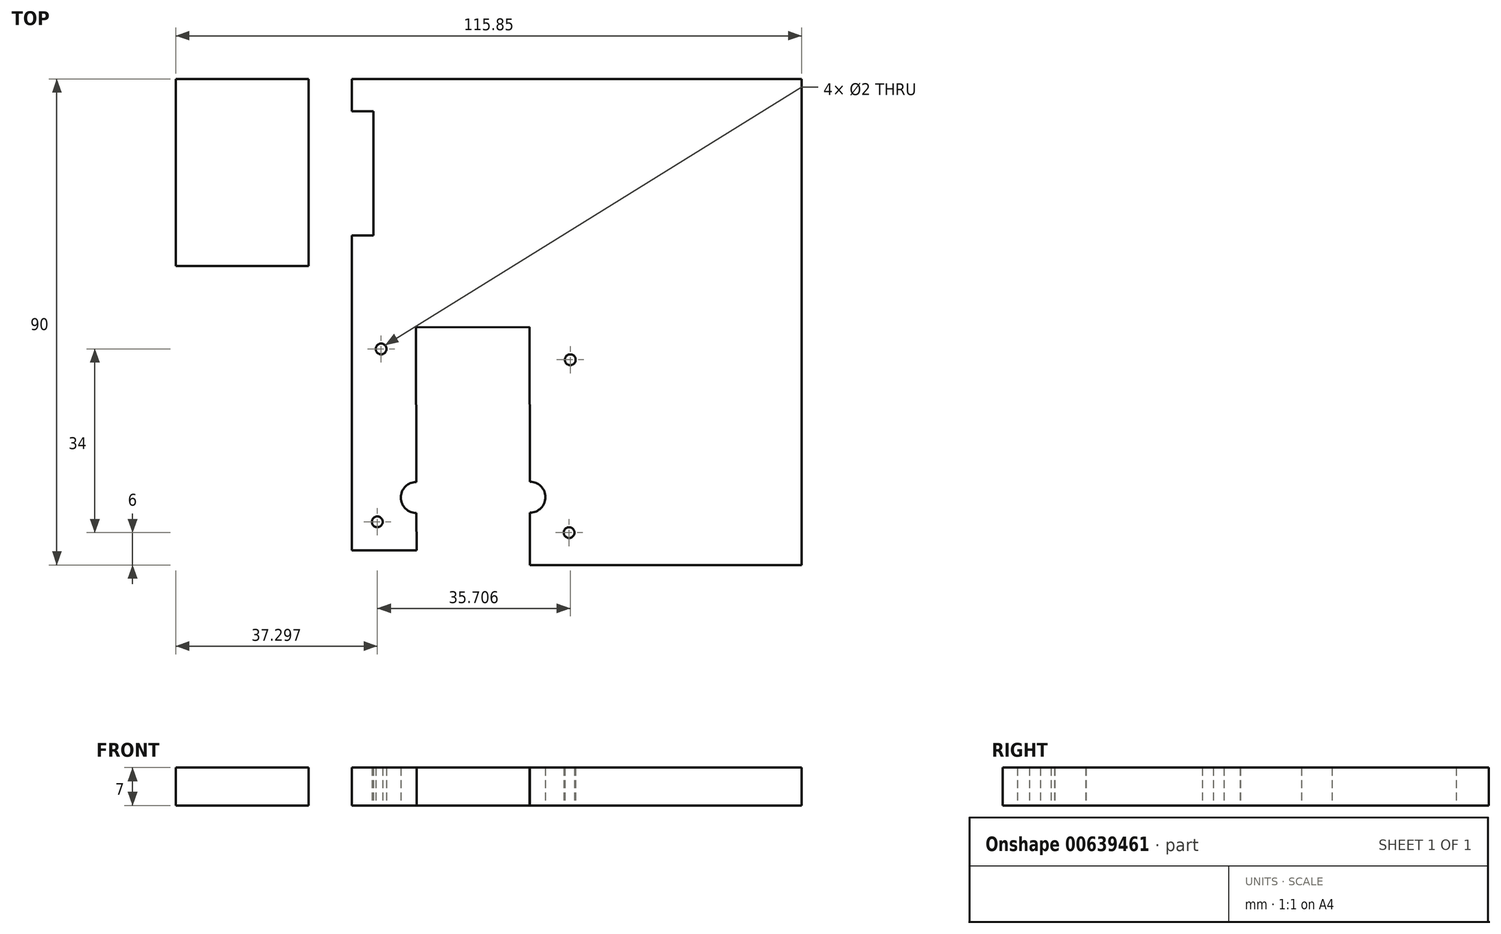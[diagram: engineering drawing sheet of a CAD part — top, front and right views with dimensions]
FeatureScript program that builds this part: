
annotation { "Feature Type Name" : "Feature", "Feature Type Description" : "" }
export const myFeature = defineFeature(function(context is Context, id is Id, definition is map)
    precondition{}
    {
        {
            var Q0;
            Q0=qCreatedBy(makeId("Top.planeOp"),FACE);
            var sketch = newSketch(context, id + "F0", { "sketchPlane" : qUnion([Q0])});
            skLineSegment(sketch, "E0.bottom", {"start": v(22.5, -45) * mm, "end": v(10.5, -45) * mm});
            skLineSegment(sketch, "E0.top", {"start": v(22.5, 45) * mm, "end": v(-22.5, 45) * mm});
            skLineSegment(sketch, "E0.left", {"start": v(22.5, -45) * mm, "end": v(22.5, 45) * mm});
            skLineSegment(sketch, "E0.right", {"start": v(-22.5, -42.25) * mm, "end": v(-22.5, 45) * mm});
            skPoint(sketch, "E0.middle", {"position": v(0, 0) * mm});
            skLineSegment(sketch, "E1.bottom", {"start": v(-10.63, -1) * mm, "end": v(10.37, -0.94) * mm});
            skLineSegment(sketch, "E1.left", {"start": v(-10.63, -1) * mm, "end": v(-10.5, -42.25) * mm});
            skLineSegment(sketch, "E1.right", {"start": v(10.37, -0.94) * mm, "end": v(10.5, -45) * mm});
            skLineSegment(sketch, "E2.bottom", {"start": v(-22.5, 39) * mm, "end": v(-14.5, 39) * mm});
            skLineSegment(sketch, "E2.top", {"start": v(-22.5, 45) * mm, "end": v(-14.5, 45) * mm});
            skLineSegment(sketch, "E2.left", {"start": v(-22.5, 39) * mm, "end": v(-22.5, 45) * mm});
            skLineSegment(sketch, "E2.right", {"start": v(-14.5, 39) * mm, "end": v(-14.5, 45) * mm});
            skLineSegment(sketch, "E3.bottom", {"start": v(-22.5, 16) * mm, "end": v(-14.5, 16) * mm});
            skLineSegment(sketch, "E3.top", {"start": v(-22.5, 10.36) * mm, "end": v(-14.5, 10.36) * mm});
            skLineSegment(sketch, "E3.left", {"start": v(-22.5, 16) * mm, "end": v(-22.5, 10.36) * mm});
            skLineSegment(sketch, "E3.right", {"start": v(-14.5, 16) * mm, "end": v(-14.5, 10.36) * mm});
            skPoint(sketch, "E4", {"position": v(-17.77, -37) * mm});
            skPoint(sketch, "E5", {"position": v(-17.07, -5) * mm});
            skPoint(sketch, "E6", {"position": v(17.93, -7) * mm});
            skPoint(sketch, "E7", {"position": v(17.73, -39) * mm});
            skPoint(sketch, "E8.positionSnap0", {"position": v(-18.5, 45) * mm});
            skPoint(sketch, "E9.positionSnap0", {"position": v(-18.5, 16) * mm});
            skPoint(sketch, "E10", {"position": v(-10.54, -32.5) * mm});
            skPoint(sketch, "E11", {"position": v(0, 45) * mm});
            skPoint(sketch, "E12", {"position": v(22.5, 17.15) * mm});
            skLineSegment(sketch, "E13", {"start": v(0, 45) * mm, "end": v(22.5, 17.15) * mm});
            skPoint(sketch, "E14", {"position": v(10.46, -32.44) * mm});
            skLineSegment(sketch, "E15", {"start": v(0, -64.42) * mm, "end": v(0, 71.46) * mm, "construction": true});
            skPoint(sketch, "E16", {"position": v(-22.5, -39) * mm});
            skPoint(sketch, "E17", {"position": v(-22.5, -42.25) * mm});
            skLineSegment(sketch, "E18", {"start": v(-22.5, -42.25) * mm, "end": v(-10.5, -42.25) * mm});
            skPoint(sketch, "E19.trimOffspring.end.orphan", {"position": v(-22.5, -45) * mm});
            skLineSegment(sketch, "E20.MirrorCS", {"start": v(-30.5, 16) * mm, "end": v(-30.5, 10.36) * mm});
            skLineSegment(sketch, "E21.MirrorCS", {"start": v(-22.5, 10.36) * mm, "end": v(-30.5, 10.36) * mm});
            skLineSegment(sketch, "E22", {"start": v(-22.5, 16) * mm, "end": v(-30.5, 16) * mm});
            skLineSegment(sketch, "E23.MirrorCS", {"start": v(-22.5, 39) * mm, "end": v(-30.5, 39) * mm});
            skLineSegment(sketch, "E24.MirrorCS", {"start": v(-30.5, 39) * mm, "end": v(-30.5, 45) * mm});
            skLineSegment(sketch, "E25", {"start": v(-22.5, 45) * mm, "end": v(-30.5, 45) * mm});
            skLineSegment(sketch, "E26", {"start": v(-14.5, 39) * mm, "end": v(-14.5, 16) * mm});
            skLineSegment(sketch, "E27", {"start": v(-30.5, 39) * mm, "end": v(-30.5, 16) * mm});
            skLineSegment(sketch, "E28", {"start": v(-30.5, 10.36) * mm, "end": v(-55.07, 10.36) * mm});
            skLineSegment(sketch, "E29", {"start": v(-55.07, 10.36) * mm, "end": v(-55.07, 45) * mm});
            skLineSegment(sketch, "E30", {"start": v(-55.07, 45) * mm, "end": v(-30.5, 45) * mm});
            skLineSegment(sketch, "E31", {"start": v(22.5, 45) * mm, "end": v(60.78, 45) * mm});
            skLineSegment(sketch, "E32", {"start": v(60.78, 45) * mm, "end": v(60.78, -10.65) * mm});
            skLineSegment(sketch, "E33", {"start": v(60.78, -10.65) * mm, "end": v(22.5, -10.65) * mm});
            skLineSegment(sketch, "E34", {"start": v(-55.07, 45) * mm, "end": v(-55.07, 56.77) * mm});
            skLineSegment(sketch, "E35", {"start": v(-55.07, 56.77) * mm, "end": v(60.64, 56.77) * mm});
            skLineSegment(sketch, "E36", {"start": v(60.64, 56.77) * mm, "end": v(60.78, 45) * mm});
            skPoint(sketch, "E37", {"position": v(-18.5, 39) * mm});
            skLineSegment(sketch, "E38", {"start": v(-18.5, 39) * mm, "end": v(-18.5, 16) * mm});
            skLineSegment(sketch, "E39", {"start": v(22.5, -45) * mm, "end": v(60.78, -45) * mm});
            skLineSegment(sketch, "E40", {"start": v(60.78, -45) * mm, "end": v(60.78, -10.65) * mm});
            skSolve(sketch);
        }
        {
            var Q0;
            Q0=makeQuery(id+"F0.imprint","IMPRINT",FACE,{"disambiguationData":[TD([[makeQuery(id+"F0.imprint","IMPRINT",EDGE,{"derivedFrom":sQuery(id+"F0.wireOp",EDGE,"E0.bottom")}),-1.0]])]});
            var Q1;
            {var subQ3=sQuery(id+"F0.wireOp",EDGE,"E13");Q1=makeQuery(id+"F0.imprint","IMPRINT",FACE,{"disambiguationData":[TD([[makeQuery(id+"F0.imprint","IMPRINT",EDGE,{"derivedFrom":subQ3}),1.0]])]});}
            var Q2;
            Q2=makeQuery(id+"F0.imprint","IMPRINT",FACE,{"disambiguationData":[TD([[makeQuery(id+"F0.imprint","IMPRINT",EDGE,{"derivedFrom":sQuery(id+"F0.wireOp",EDGE,"E20.MirrorCS")}),-1.0]])]});
            var Q3;
            Q3=makeQuery(id+"F0.imprint","IMPRINT",FACE,{"disambiguationData":[TD([[makeQuery(id+"F0.imprint","IMPRINT",EDGE,{"derivedFrom":sQuery(id+"F0.wireOp",EDGE,"E2.left")}),1.0]])]});
            var Q4;
            Q4=makeQuery(id+"F0.imprint","IMPRINT",FACE,{"disambiguationData":[TD([[makeQuery(id+"F0.imprint","IMPRINT",EDGE,{"derivedFrom":sQuery(id+"F0.wireOp",EDGE,"E2.bottom")}),1.0]])]});
            var Q5;
            Q5=makeQuery(id+"F0.imprint","IMPRINT",FACE,{"disambiguationData":[TD([[makeQuery(id+"F0.imprint","IMPRINT",EDGE,{"derivedFrom":sQuery(id+"F0.wireOp",EDGE,"E3.bottom")}),-1.0]])]});
            var Q6;
            Q6=makeQuery(id+"F0.imprint","IMPRINT",FACE,{"disambiguationData":[TD([[makeQuery(id+"F0.imprint","IMPRINT",EDGE,{"derivedFrom":sQuery(id+"F0.wireOp",EDGE,"E3.left")}),-1.0]])]});
            var Q7;
            {var subQ0=sQuery(id+"F0.wireOp",EDGE,"E31");Q7=makeQuery(id+"F0.imprint","IMPRINT",FACE,{"disambiguationData":[TD([[makeQuery(id+"F0.imprint","IMPRINT",EDGE,{"derivedFrom":subQ0}),-1.0]])]});}
            var Q8;
            {var subQ0=sQuery(id+"F0.wireOp",EDGE,"E2.top");Q8=makeQuery(id+"F0.imprint","IMPRINT",FACE,{"disambiguationData":[TD([[makeQuery(id+"F0.imprint","IMPRINT",EDGE,{"derivedFrom":subQ0}),1.0]])]});}
            var Q9;
            {var subQ0=sQuery(id+"F0.wireOp",EDGE,"E26");Q9=makeQuery(id+"F0.imprint","IMPRINT",FACE,{"disambiguationData":[TD([[makeQuery(id+"F0.imprint","IMPRINT",EDGE,{"derivedFrom":subQ0}),-1.0]])]});}
            var Q10;
            {var subQ2=sQuery(id+"F0.wireOp",EDGE,"E33");Q10=makeQuery(id+"F0.imprint","IMPRINT",FACE,{"disambiguationData":[TD([[makeQuery(id+"F0.imprint","IMPRINT",EDGE,{"derivedFrom":subQ2}),1.0]])]});}
            extrude(context, id + "F1", {"entities" : qUnion([Q0, Q1, Q2, Q3, Q4, Q5, Q6, Q7, Q8, Q9, Q10]), "depth" : 7 * mm, "offsetDistance" : 25 * mm});
        }
        {
            var Q0;
            Q0=sQuery(id+"F0.wireOp",VERTEX,"E5");
            var Q1;
            Q1=sQuery(id+"F0.wireOp",VERTEX,"E4");
            var Q2;
            Q2=sQuery(id+"F0.wireOp",VERTEX,"E7");
            var Q3;
            Q3=sQuery(id+"F0.wireOp",VERTEX,"E6");
            var Q4;
            Q4=makeQuery(id+"F1.opExtrude","SWEPT_BODY",BODY,{"disambiguationData":[OSD([sQuery(id+"F0.wireOp",EDGE,"E0.bottom"),sQuery(id+"F0.wireOp",EDGE,"E0.top"),sQuery(id+"F0.wireOp",EDGE,"E0.left"),sQuery(id+"F0.wireOp",EDGE,"E0.right"),sQuery(id+"F0.wireOp",EDGE,"E1.bottom"),sQuery(id+"F0.wireOp",EDGE,"E1.left"),sQuery(id+"F0.wireOp",EDGE,"E1.right"),sQuery(id+"F0.wireOp",EDGE,"E2.bottom"),sQuery(id+"F0.wireOp",EDGE,"E2.right"),sQuery(id+"F0.wireOp",EDGE,"E3.bottom"),sQuery(id+"F0.wireOp",EDGE,"E3.top"),sQuery(id+"F0.wireOp",EDGE,"E3.right"),sQuery(id+"F0.wireOp",EDGE,"E19.trimOffspring")])]});
            hole(context, id + "F2", {"style" : HoleStyle.SIMPLE, "endStyle" : HoleEndStyle.THROUGH, "oppositeDirection" : true, "holeDiameter" : 2 * mm, "isTappedThrough" : true, "tappedDepth" : 12.7 * mm, "tapClearance" : 3, "locations" : qUnion([Q0, Q1, Q2, Q3]), "scope" : qUnion([Q4])});
        }
        {
            var Q0;
            Q0=sQuery(id+"F0.wireOp",VERTEX,"E10");
            var Q1;
            Q1=sQuery(id+"F0.wireOp",VERTEX,"E14");
            var Q2;
            Q2=makeQuery(id+"F1.opExtrude","SWEPT_BODY",BODY,{"disambiguationData":[OSD([sQuery(id+"F0.wireOp",EDGE,"E0.bottom"),sQuery(id+"F0.wireOp",EDGE,"E0.top"),sQuery(id+"F0.wireOp",EDGE,"E0.left"),sQuery(id+"F0.wireOp",EDGE,"E0.right"),sQuery(id+"F0.wireOp",EDGE,"E1.bottom"),sQuery(id+"F0.wireOp",EDGE,"E1.left"),sQuery(id+"F0.wireOp",EDGE,"E1.right"),sQuery(id+"F0.wireOp",EDGE,"E2.bottom"),sQuery(id+"F0.wireOp",EDGE,"E2.right"),sQuery(id+"F0.wireOp",EDGE,"E3.bottom"),sQuery(id+"F0.wireOp",EDGE,"E3.top"),sQuery(id+"F0.wireOp",EDGE,"E3.right"),sQuery(id+"F0.wireOp",EDGE,"E19.trimOffspring")])]});
            hole(context, id + "F3", {"style" : HoleStyle.SIMPLE, "endStyle" : HoleEndStyle.THROUGH, "oppositeDirection" : true, "holeDiameter" : 5.75 * mm, "isTappedThrough" : true, "tappedDepth" : 12.7 * mm, "tapClearance" : 3, "locations" : qUnion([Q0, Q1]), "scope" : qUnion([Q2])});
        }
    });
